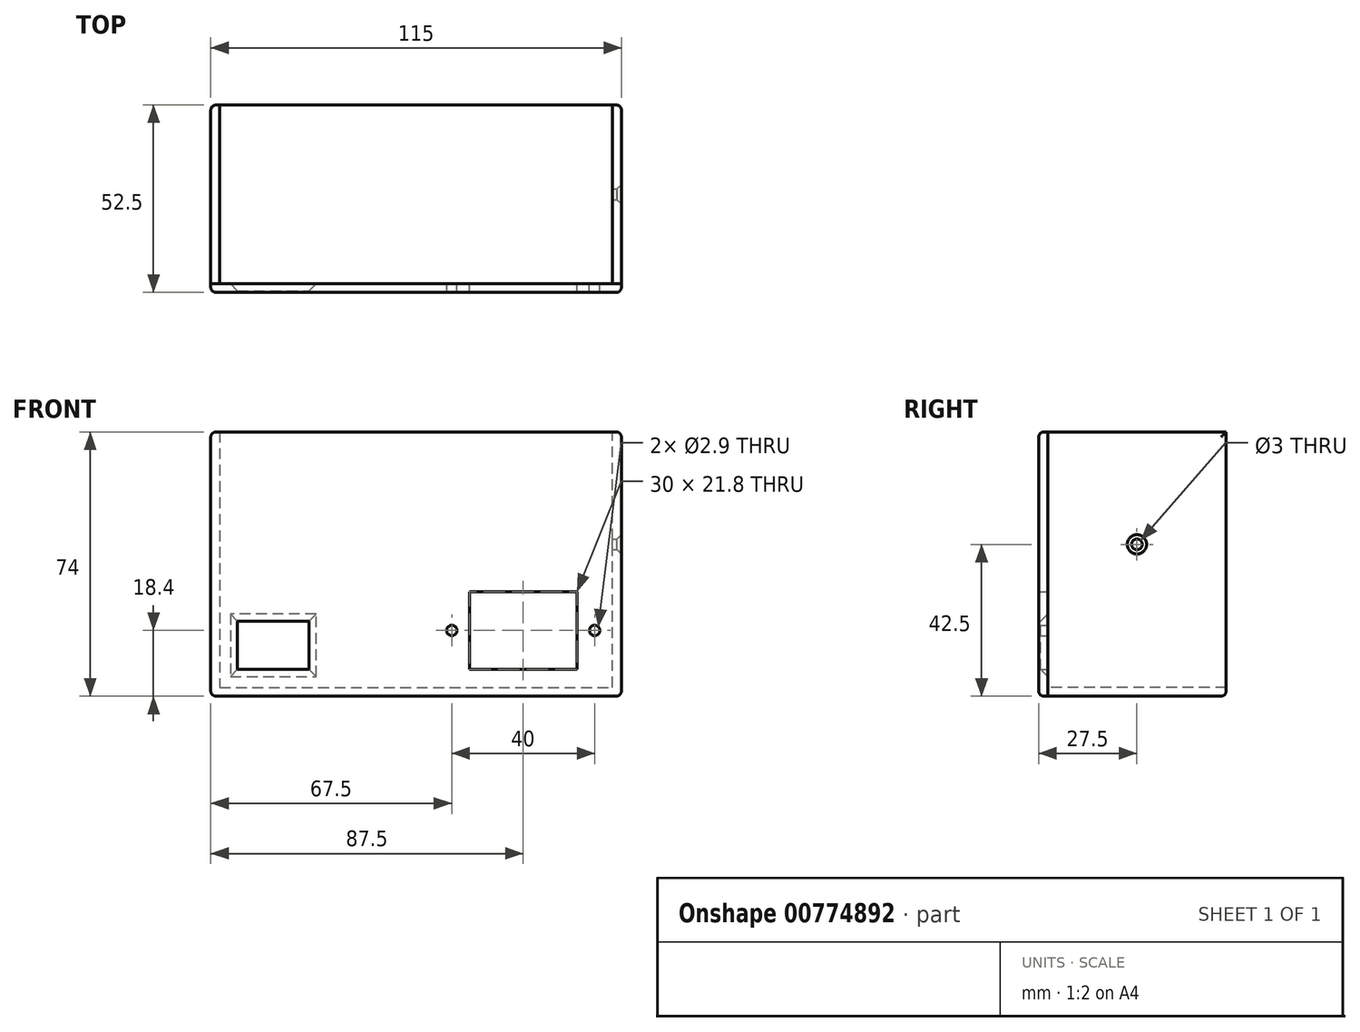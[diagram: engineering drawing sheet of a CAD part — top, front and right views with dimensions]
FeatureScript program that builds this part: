
annotation { "Feature Type Name" : "Feature", "Feature Type Description" : "" }
export const myFeature = defineFeature(function(context is Context, id is Id, definition is map)
    precondition{}
    {
        {
            var Q0;
            Q0=qCreatedBy(makeId("Front.planeOp"),FACE);
            var sketch = newSketch(context, id + "F0", { "sketchPlane" : qUnion([Q0])});
            skLineSegment(sketch, "E0.bottom", {"start": v(57.5, 37) * mm, "end": v(-57.5, 37) * mm});
            skLineSegment(sketch, "E0.top", {"start": v(57.5, -37) * mm, "end": v(-57.5, -37) * mm});
            skLineSegment(sketch, "E0.left", {"start": v(57.5, 37) * mm, "end": v(57.5, -37) * mm});
            skLineSegment(sketch, "E0.right", {"start": v(-57.5, 37) * mm, "end": v(-57.5, -37) * mm});
            skPoint(sketch, "E0.middle", {"position": v(0, 0) * mm});
            skLineSegment(sketch, "E1.bottom", {"start": v(-55, 34.5) * mm, "end": v(55, 34.5) * mm, "construction": true});
            skLineSegment(sketch, "E1.top", {"start": v(-55, -34.5) * mm, "end": v(55, -34.5) * mm, "construction": true});
            skLineSegment(sketch, "E1.left", {"start": v(-55, 34.5) * mm, "end": v(-55, -34.5) * mm, "construction": true});
            skLineSegment(sketch, "E1.right", {"start": v(55, 34.5) * mm, "end": v(55, -34.5) * mm, "construction": true});
            skLineSegment(sketch, "E2.bottom", {"start": v(55, 34.5) * mm, "end": v(-55, 34.5) * mm, "construction": true});
            skLineSegment(sketch, "E2.top", {"start": v(55, 5.5) * mm, "end": v(-55, 5.5) * mm, "construction": true});
            skLineSegment(sketch, "E2.left", {"start": v(55, 34.5) * mm, "end": v(55, 5.5) * mm, "construction": true});
            skLineSegment(sketch, "E2.right", {"start": v(-55, 34.5) * mm, "end": v(-55, 5.5) * mm, "construction": true});
            skLineSegment(sketch, "E3.bottom", {"start": v(15, -7.7) * mm, "end": v(45, -7.7) * mm});
            skLineSegment(sketch, "E3.top", {"start": v(15, -29.5) * mm, "end": v(45, -29.5) * mm});
            skLineSegment(sketch, "E3.left", {"start": v(15, -7.7) * mm, "end": v(15, -29.5) * mm});
            skLineSegment(sketch, "E3.right", {"start": v(45, -7.7) * mm, "end": v(45, -29.5) * mm});
            skCircle(sketch, "E4", {"center": v(10, -18.6) * mm, "radius": 1.45 * mm});
            skPoint(sketch, "E4.centerSnap0", {"position": v(15, -18.6) * mm});
            skCircle(sketch, "E5", {"center": v(50, -18.6) * mm, "radius": 1.45 * mm});
            skLineSegment(sketch, "E6", {"start": v(10, -18.6) * mm, "end": v(50, -18.6) * mm, "construction": true});
            skLineSegment(sketch, "E7", {"start": v(10, -18.6) * mm, "end": v(15, -18.6) * mm, "construction": true});
            skLineSegment(sketch, "E8.bottom", {"start": v(-50, -16) * mm, "end": v(-30, -16) * mm});
            skLineSegment(sketch, "E8.top", {"start": v(-50, -29.5) * mm, "end": v(-30, -29.5) * mm});
            skLineSegment(sketch, "E8.left", {"start": v(-50, -16) * mm, "end": v(-50, -29.5) * mm});
            skLineSegment(sketch, "E8.right", {"start": v(-30, -16) * mm, "end": v(-30, -29.5) * mm});
            skLineSegment(sketch, "E9.bottom", {"start": v(-55, 34.5) * mm, "end": v(55, 34.5) * mm});
            skLineSegment(sketch, "E9.top", {"start": v(-55, -34.5) * mm, "end": v(55, -34.5) * mm});
            skLineSegment(sketch, "E9.left", {"start": v(-55, 34.5) * mm, "end": v(-55, -34.5) * mm});
            skLineSegment(sketch, "E9.right", {"start": v(55, 34.5) * mm, "end": v(55, -34.5) * mm});
            skLineSegment(sketch, "E10", {"start": v(-55, 34.5) * mm, "end": v(-55, 37) * mm});
            skLineSegment(sketch, "E11", {"start": v(55, 34.5) * mm, "end": v(55, 37) * mm});
            skSolve(sketch);
        }
        {
            var Q0;
            Q0=makeQuery(id+"F0.imprint","IMPRINT",FACE,{"disambiguationData":[TD([[makeQuery(id+"F0.imprint","IMPRINT",EDGE,{"derivedFrom":sQuery(id+"F0.wireOp",EDGE,"E3.bottom")}),1.0]])]});
            var Q1;
            Q1=makeQuery(id+"F0.imprint","IMPRINT",FACE,{"disambiguationData":[TD([[makeQuery(id+"F0.imprint","IMPRINT",EDGE,{"derivedFrom":sQuery(id+"F0.wireOp",EDGE,"E0.top")}),-1.0]])]});
            var Q2;
            Q2=makeQuery(id+"F0.imprint","IMPRINT",FACE,{"disambiguationData":[TD([[makeQuery(id+"F0.imprint","IMPRINT",EDGE,{"derivedFrom":sQuery(id+"F0.wireOp",EDGE,"E9.bottom")}),1.0]])]});
            extrude(context, id + "F1", {"entities" : qUnion([Q0, Q1, Q2]), "depth" : 2.5 * mm, "offsetDistance" : 25 * mm});
        }
        {
            var Q0;
            Q0=makeQuery(id+"F0.imprint","IMPRINT",FACE,{"disambiguationData":[TD([[makeQuery(id+"F0.imprint","IMPRINT",EDGE,{"derivedFrom":sQuery(id+"F0.wireOp",EDGE,"E0.top")}),-1.0]])]});
            extrude(context, id + "F2", {"entities" : qUnion([Q0]), "depth" : -50 * mm, "offsetDistance" : 25 * mm});
        }
        {
            var Q0;
            Q0=makeQuery(id+"F2.opExtrude","SWEPT_FACE",FACE,{"disambiguationData":[OSD([sQuery(id+"F0.wireOp",EDGE,"E0.left")])]});
            var sketch = newSketch(context, id + "F3", { "sketchPlane" : qUnion([Q0])});
            skLineSegment(sketch, "E12", {"start": v(25, 37) * mm, "end": v(25, 5.5) * mm, "construction": true});
            skSolve(sketch);
        }
        {
            var Q0;
            Q0=sQuery(id+"F3.wireOp",VERTEX,"E12.end");
            var Q1;
            Q1=makeQuery(id+"F2.opExtrude","SWEPT_BODY",BODY,{"disambiguationData":[OSD([sQuery(id+"F0.wireOp",EDGE,"E0.bottom"),sQuery(id+"F0.wireOp",EDGE,"E0.top"),sQuery(id+"F0.wireOp",EDGE,"E0.left"),sQuery(id+"F0.wireOp",EDGE,"E0.right"),sQuery(id+"F0.wireOp",EDGE,"E9.top"),sQuery(id+"F0.wireOp",EDGE,"E9.left"),sQuery(id+"F0.wireOp",EDGE,"E9.right"),sQuery(id+"F0.wireOp",EDGE,"E10"),sQuery(id+"F0.wireOp",EDGE,"E11")])]});
            hole(context, id + "F4", {"style" : HoleStyle.C_SINK, "endStyle" : HoleEndStyle.BLIND, "holeDiameter" : 3 * mm, "cSinkDiameter" : 5.4 * mm, "cSinkAngle" : 90 * degree, "majorDiameter" : 5 * mm, "holeDepth" : 12 * mm, "isTappedThrough" : true, "tappedDepth" : 12 * mm, "tapClearance" : 3, "locations" : qUnion([Q0]), "scope" : qUnion([Q1])});
        }
        {
            var Q0;
            Q0=makeQuery(id+"F1.opExtrude","CAP_EDGE",EDGE,{"disambiguationData":[OSD([sQuery(id+"F0.wireOp",EDGE,"E8.right")])],"isStart":true});
            var Q1;
            Q1=makeQuery(id+"F1.opExtrude","CAP_EDGE",EDGE,{"disambiguationData":[OSD([sQuery(id+"F0.wireOp",EDGE,"E8.bottom")])],"isStart":true});
            var Q2;
            Q2=makeQuery(id+"F1.opExtrude","CAP_EDGE",EDGE,{"disambiguationData":[OSD([sQuery(id+"F0.wireOp",EDGE,"E8.top")])],"isStart":true});
            var Q3;
            Q3=makeQuery(id+"F1.opExtrude","CAP_EDGE",EDGE,{"disambiguationData":[OSD([sQuery(id+"F0.wireOp",EDGE,"E8.left")])],"isStart":true});
            chamfer(context, id + "F5", {"entities" : qUnion([Q0, Q1, Q2, Q3]), "width" : 2 * mm, "tangentPropagation" : true});
        }
        {
            var Q0;
            Q0=makeQuery(id+"F2.opExtrude","SWEPT_EDGE",EDGE,{"disambiguationData":[OSD([sQuery(id+"F0.wireOp",EDGE,"E0.bottom"),sQuery(id+"F0.wireOp",EDGE,"E0.right")])]});
            var Q1;
            Q1=makeQuery(id+"F1.opExtrude","SWEPT_EDGE",EDGE,{"disambiguationData":[OSD([sQuery(id+"F0.wireOp",EDGE,"E0.bottom"),sQuery(id+"F0.wireOp",EDGE,"E0.right")])]});
            var Q2;
            Q2=makeQuery(id+"F1.opExtrude","CAP_EDGE",EDGE,{"disambiguationData":[OSD([sQuery(id+"F0.wireOp",EDGE,"E0.right")])],"isStart":false});
            var Q3;
            Q3=makeQuery(id+"F1.opExtrude","CAP_EDGE",EDGE,{"disambiguationData":[OSD([sQuery(id+"F0.wireOp",EDGE,"E0.bottom")])],"isStart":false});
            var Q4;
            Q4=makeQuery(id+"F1.opExtrude","SWEPT_EDGE",EDGE,{"disambiguationData":[OSD([sQuery(id+"F0.wireOp",EDGE,"E0.top"),sQuery(id+"F0.wireOp",EDGE,"E0.right")])]});
            var Q5;
            Q5=makeQuery(id+"F2.opExtrude","SWEPT_EDGE",EDGE,{"disambiguationData":[OSD([sQuery(id+"F0.wireOp",EDGE,"E0.top"),sQuery(id+"F0.wireOp",EDGE,"E0.right")])]});
            var Q6;
            Q6=makeQuery(id+"F1.opExtrude","CAP_EDGE",EDGE,{"disambiguationData":[OSD([sQuery(id+"F0.wireOp",EDGE,"E0.top")])],"isStart":false});
            var Q7;
            Q7=makeQuery(id+"F1.opExtrude","CAP_EDGE",EDGE,{"disambiguationData":[OSD([sQuery(id+"F0.wireOp",EDGE,"E0.left")])],"isStart":false});
            var Q8;
            Q8=makeQuery(id+"F1.opExtrude","SWEPT_EDGE",EDGE,{"disambiguationData":[OSD([sQuery(id+"F0.wireOp",EDGE,"E0.bottom"),sQuery(id+"F0.wireOp",EDGE,"E0.left")])]});
            var Q9;
            Q9=makeQuery(id+"F2.opExtrude","SWEPT_EDGE",EDGE,{"disambiguationData":[OSD([sQuery(id+"F0.wireOp",EDGE,"E0.bottom"),sQuery(id+"F0.wireOp",EDGE,"E0.left")])]});
            var Q10;
            Q10=makeQuery(id+"F1.opExtrude","SWEPT_EDGE",EDGE,{"disambiguationData":[OSD([sQuery(id+"F0.wireOp",EDGE,"E0.top"),sQuery(id+"F0.wireOp",EDGE,"E0.left")])]});
            var Q11;
            Q11=makeQuery(id+"F2.opExtrude","SWEPT_EDGE",EDGE,{"disambiguationData":[OSD([sQuery(id+"F0.wireOp",EDGE,"E0.top"),sQuery(id+"F0.wireOp",EDGE,"E0.left")])]});
            var Q12;
            Q12=makeQuery(id+"F2.opExtrude","CAP_EDGE",EDGE,{"disambiguationData":[OSD([sQuery(id+"F0.wireOp",EDGE,"E0.left")])],"isStart":false});
            var Q13;
            Q13=makeQuery(id+"F2.opExtrude","CAP_EDGE",EDGE,{"disambiguationData":[OSD([sQuery(id+"F0.wireOp",EDGE,"E0.right")])],"isStart":false});
            var Q14;
            Q14=makeQuery(id+"F2.opExtrude","CAP_EDGE",EDGE,{"disambiguationData":[OSD([sQuery(id+"F0.wireOp",EDGE,"E0.top")])],"isStart":false});
            fillet(context, id + "F6", {"entities" : qUnion([Q0, Q1, Q2, Q3, Q4, Q5, Q6, Q7, Q8, Q9, Q10, Q11, Q12, Q13, Q14]), "radius" : 1.5 * mm, "tangentPropagation" : true, "allowEdgeOverflow" : false});
        }
    });
